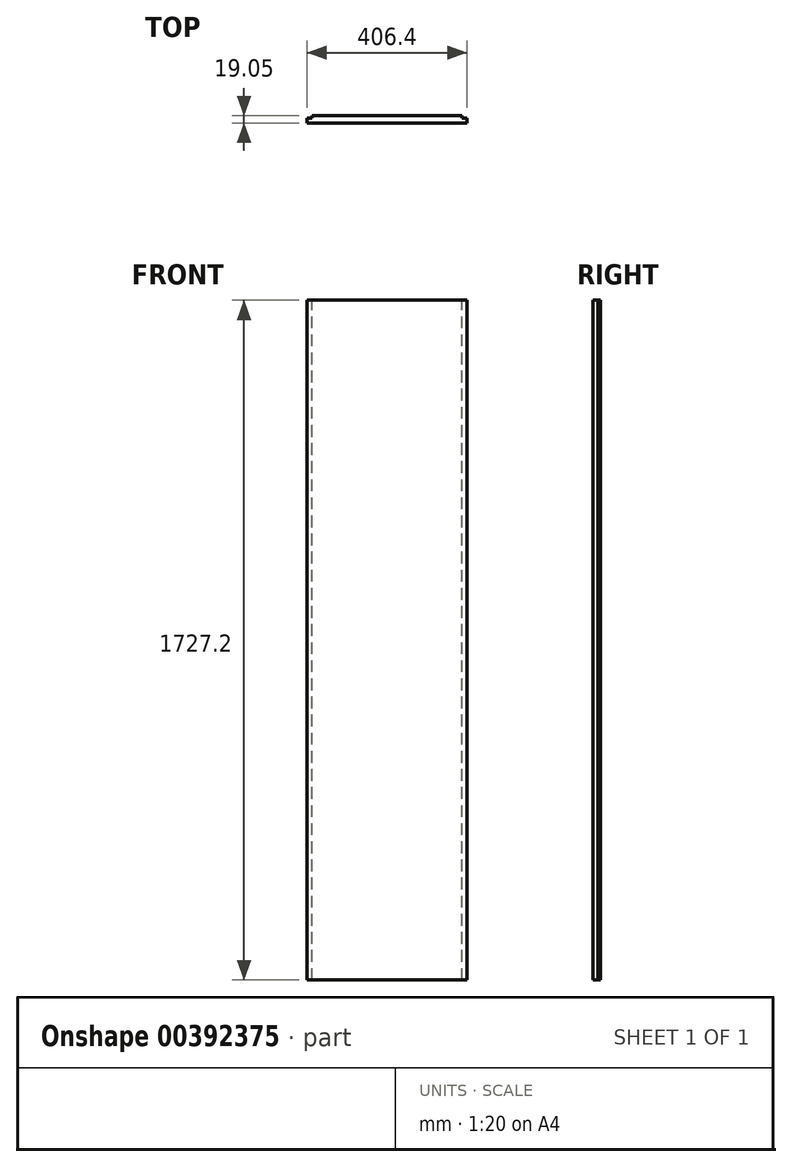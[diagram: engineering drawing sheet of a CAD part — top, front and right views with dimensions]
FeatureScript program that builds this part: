
annotation { "Feature Type Name" : "Feature", "Feature Type Description" : "" }
export const myFeature = defineFeature(function(context is Context, id is Id, definition is map)
    precondition{}
    {
        {
            var Q0;
            Q0=qCreatedBy(makeId("Top.planeOp"),FACE);
            var sketch = newSketch(context, id + "F0", { "sketchPlane" : qUnion([Q0])});
            skLineSegment(sketch, "E0.bottom", {"start": v(-203.2, 0) * mm, "end": v(203.2, 0) * mm});
            skLineSegment(sketch, "E0.top", {"start": v(-203.2, -19.05) * mm, "end": v(203.2, -19.05) * mm});
            skLineSegment(sketch, "E0.left", {"start": v(-203.2, 0) * mm, "end": v(-203.2, -19.05) * mm});
            skLineSegment(sketch, "E0.right", {"start": v(203.2, 0) * mm, "end": v(203.2, -19.05) * mm});
            skSolve(sketch);
        }
        {
            var Q0;
            Q0=qSketchRegion(id+"F0",true);
            extrude(context, id + "F1", {"entities" : qUnion([Q0]), "depth" : 1727.2 * mm});
        }
        {
            var Q0;
            Q0=makeQuery(id+"F1.opExtrude","CAP_FACE",FACE,{"disambiguationData":[OSD([sQuery(id+"F0.wireOp",EDGE,"E0.bottom"),sQuery(id+"F0.wireOp",EDGE,"E0.top"),sQuery(id+"F0.wireOp",EDGE,"E0.left"),sQuery(id+"F0.wireOp",EDGE,"E0.right")])],"isStart":false});
            var sketch = newSketch(context, id + "F2", { "sketchPlane" : qUnion([Q0])});
            skLineSegment(sketch, "E1", {"start": v(232.92, -6.35) * mm, "end": v(190.5, -6.35) * mm});
            skLineSegment(sketch, "E2", {"start": v(190.5, -6.35) * mm, "end": v(190.5, 0) * mm});
            skSolve(sketch);
        }
        {
            var Q0;
            {var subQ0=sQuery(id+"F2.wireOp",EDGE,"E1");Q0=makeQuery(id+"F2.imprint","IMPRINT",FACE,{"disambiguationData":[TD([[makeQuery(id+"F2.imprint","IMPRINT",EDGE,{"derivedFrom":subQ0}),-1.0]])]});}
            var Q1;
            Q1=makeQuery(id+"F1.opExtrude","CAP_FACE",FACE,{"disambiguationData":[OSD([sQuery(id+"F0.wireOp",EDGE,"E0.bottom"),sQuery(id+"F0.wireOp",EDGE,"E0.top"),sQuery(id+"F0.wireOp",EDGE,"E0.left"),sQuery(id+"F0.wireOp",EDGE,"E0.right")])],"isStart":true});
            extrude(context, id + "F3", {"entities" : qUnion([Q0, Q1]), "operationType" : NewBodyOperationType.REMOVE, "endBound" : BoundingType.THROUGH_ALL, "oppositeDirection" : true, "depth" : 25.4 * mm});
        }
        {
            var Q0;
            Q0=makeQuery(id+"F1.opExtrude","CAP_FACE",FACE,{"disambiguationData":[OSD([sQuery(id+"F0.wireOp",EDGE,"E0.bottom"),sQuery(id+"F0.wireOp",EDGE,"E0.top"),sQuery(id+"F0.wireOp",EDGE,"E0.left"),sQuery(id+"F0.wireOp",EDGE,"E0.right")])],"isStart":false});
            var sketch = newSketch(context, id + "F4", { "sketchPlane" : qUnion([Q0])});
            skLineSegment(sketch, "E3", {"start": v(-203.2, -6.35) * mm, "end": v(-190.5, -6.35) * mm});
            skLineSegment(sketch, "E4", {"start": v(-190.5, -6.35) * mm, "end": v(-190.5, 0) * mm});
            skSolve(sketch);
        }
        {
            var Q0;
            {var subQ0=sQuery(id+"F4.wireOp",EDGE,"E3");Q0=makeQuery(id+"F4.imprint","IMPRINT",FACE,{"disambiguationData":[TD([[makeQuery(id+"F4.imprint","IMPRINT",EDGE,{"derivedFrom":subQ0}),1.0]])]});}
            extrude(context, id + "F5", {"entities" : qUnion([Q0]), "operationType" : NewBodyOperationType.REMOVE, "endBound" : BoundingType.THROUGH_ALL, "oppositeDirection" : true, "depth" : 25.4 * mm});
        }
        {
            var Q0;
            Q0=qCreatedBy(makeId("Front.planeOp"),FACE);
            var sketch = newSketch(context, id + "F6", { "sketchPlane" : qUnion([Q0])});
            skLineSegment(sketch, "E5", {"start": v(0, 0) * mm, "end": v(0, 179.09) * mm});
            skSolve(sketch);
        }
    });
